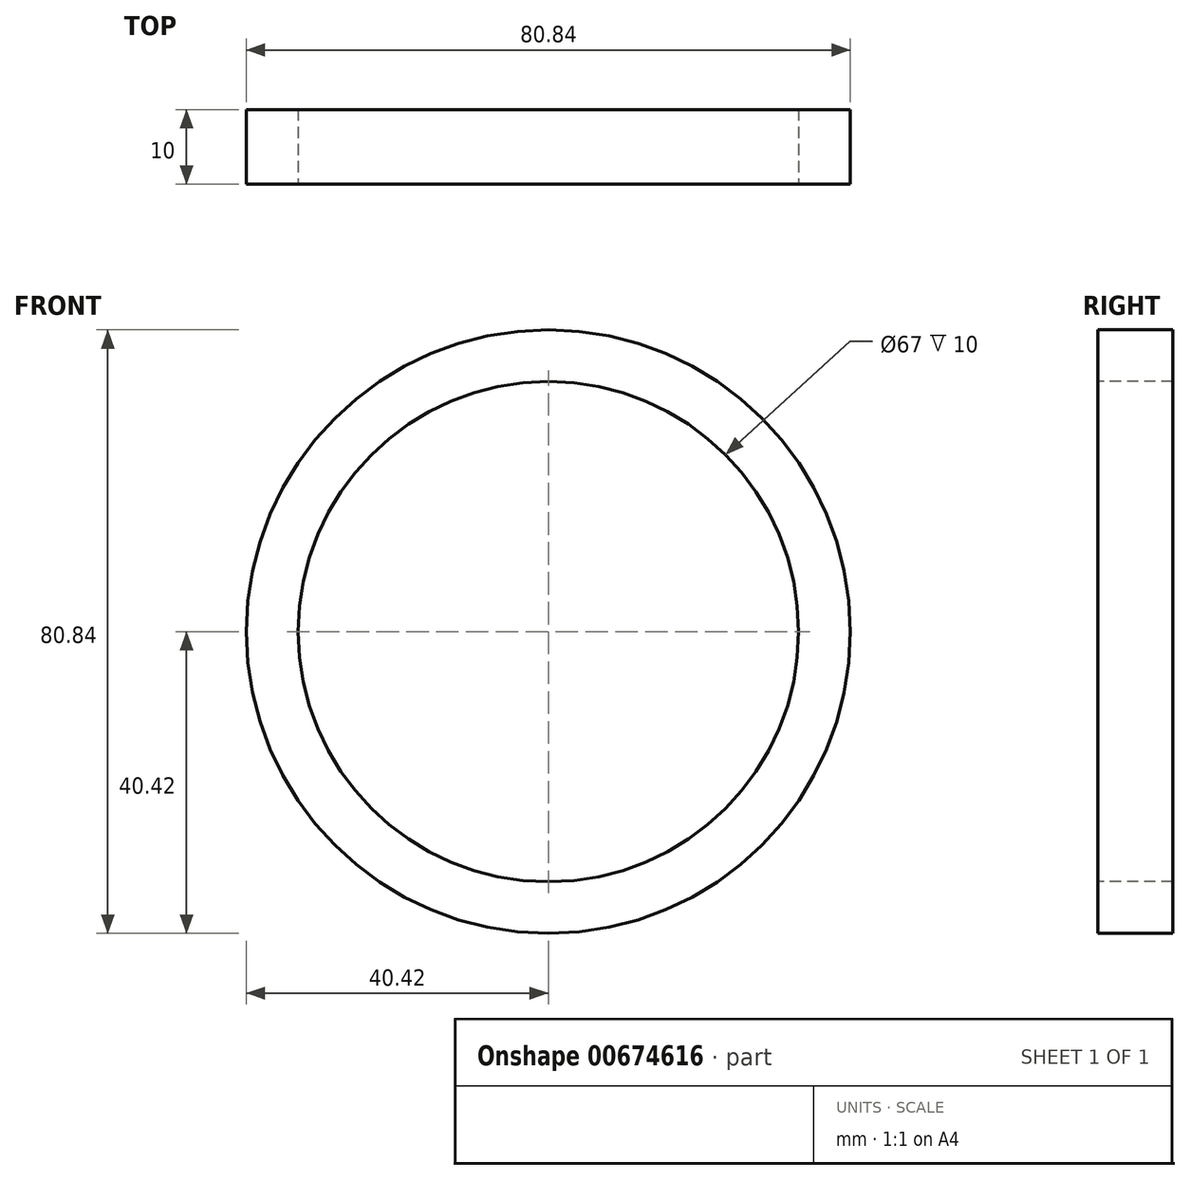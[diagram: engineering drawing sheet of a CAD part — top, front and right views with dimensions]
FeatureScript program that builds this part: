
annotation { "Feature Type Name" : "Feature", "Feature Type Description" : "" }
export const myFeature = defineFeature(function(context is Context, id is Id, definition is map)
    precondition{}
    {
        {
            var Q0;
            Q0=qCreatedBy(makeId("Front.planeOp"),FACE);
            var sketch = newSketch(context, id + "F0", { "sketchPlane" : qUnion([Q0])});
            skCircle(sketch, "E0", {"center": v(0, 0) * mm, "radius": 40.42 * mm});
            skSolve(sketch);
        }
        {
            var Q0;
            Q0=makeQuery(id+"F0.imprint","IMPRINT",FACE,{"disambiguationData":[TD([[makeQuery(id+"F0.imprint","IMPRINT",EDGE,{"derivedFrom":sQuery(id+"F0.wireOp",EDGE,"E0")}),1.0]])]});
            extrude(context, id + "F1", {"entities" : qUnion([Q0]), "depth" : 10 * mm, "offsetDistance" : 25 * mm});
        }
        {
            var Q0;
            Q0=makeQuery(id+"F1.opExtrude","CAP_FACE",FACE,{"disambiguationData":[OSD([sQuery(id+"F0.wireOp",EDGE,"E0")])],"isStart":false});
            var sketch = newSketch(context, id + "F2", { "sketchPlane" : qUnion([Q0])});
            skCircle(sketch, "E1", {"center": v(0, 0) * mm, "radius": 33.1 * mm});
            skFitSpline(sketch, "E2", {"points": [v(-5.35, 32.66) * mm, v(-12.9, 30.48) * mm, v(-22.26, 24.49) * mm, v(-28.47, 16.86) * mm, v(-32.11, 8) * mm, v(-33.1, 0) * mm, v(-32, -8.4) * mm, v(-27.94, -17.73) * mm, v(-17.53, -28.06) * mm, v(-7.95, -32.12) * mm, v(0, -33.1) * mm, v(9.74, -31.63) * mm, v(17.82, -27.88) * mm, v(24.19, -22.58) * mm, v(28.18, -17.35) * mm, v(31.33, -10.64) * mm, v(32.79, -4.49) * mm, v(33.1, 0) * mm, v(31.75, 9.32) * mm, v(28.87, 16.18) * mm, v(23.9, 22.9) * mm, v(16.78, 28.52) * mm, v(10.52, 31.37) * mm, v(3.45, 32.91) * mm, v(0, 33.1) * mm, v(-5.35, 32.66) * mm]});
            skSolve(sketch);
        }
        {
            var Q0;
            Q0=sQuery(id+"F2.wireOp",VERTEX,"E1.center");
            var Q1;
            Q1=makeQuery(id+"F1.opExtrude","SWEPT_BODY",BODY,{"disambiguationData":[OSD([sQuery(id+"F0.wireOp",EDGE,"E0")])]});
            hole(context, id + "F3", {"style" : HoleStyle.SIMPLE, "endStyle" : HoleEndStyle.THROUGH, "holeDiameter" : 67 * mm, "majorDiameter" : 5 * mm, "isTappedThrough" : true, "tappedDepth" : 12 * mm, "tapClearance" : 3, "locations" : qUnion([Q0]), "scope" : qUnion([Q1])});
        }
    });
